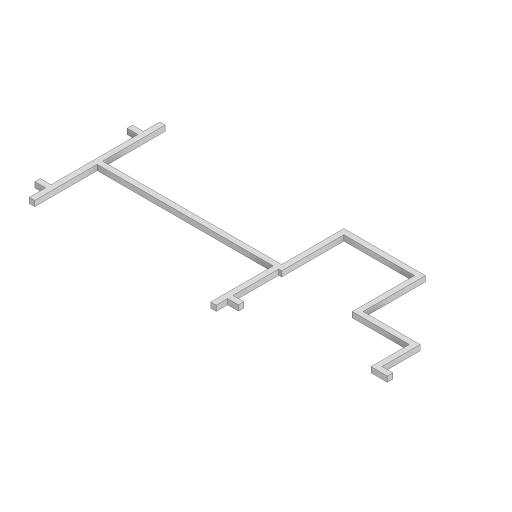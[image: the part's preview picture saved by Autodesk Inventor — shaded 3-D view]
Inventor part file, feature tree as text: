
AUTODESK INVENTOR PART (.ipt)
format: ipt  version: 2023.4 (Build 274418000, 418)  size: 180,224 bytes
history: native  units: in
note: dims shown in document units (in); Inventor stores cm internally (conversion verified against a paired STEP export)
features: extrude x1, sketch x1
ambient origin geometry x8: Origin, YZ Plane, XZ Plane, XY Plane, X Axis, Y Axis, Z Axis, Center Point
bodies: Solid1 (feature_tree)
feature tree (2):
  extrude  "Extrusion1"  Depth=4.7244in
  sketch  "Sketch1"  dims[d0=11.205in d1=4.7244in d2=0.5906in d3=0.5906in d4=0.3937in d5=0.1969in d6=0.1969in d7=0.1969in d14=0.0in d15=0.0in d17=0.4843in d18=2.2638in d19=2.2638in d20=0.1969in d26=6.7677in d30=0.1772in d34=0.7874in d36=6.8744in d37=0.1969in d38=0.1969in d39=2.5591in d40=0.1969in d41=0.0in d42=0.3858in d43=0.1969in d48=11.6972in d49=0.1969in d50=0.5906in d51=0.1772in d52=0.1969in d53=0.1969in d54=0.5906in d55=0.3937in]
